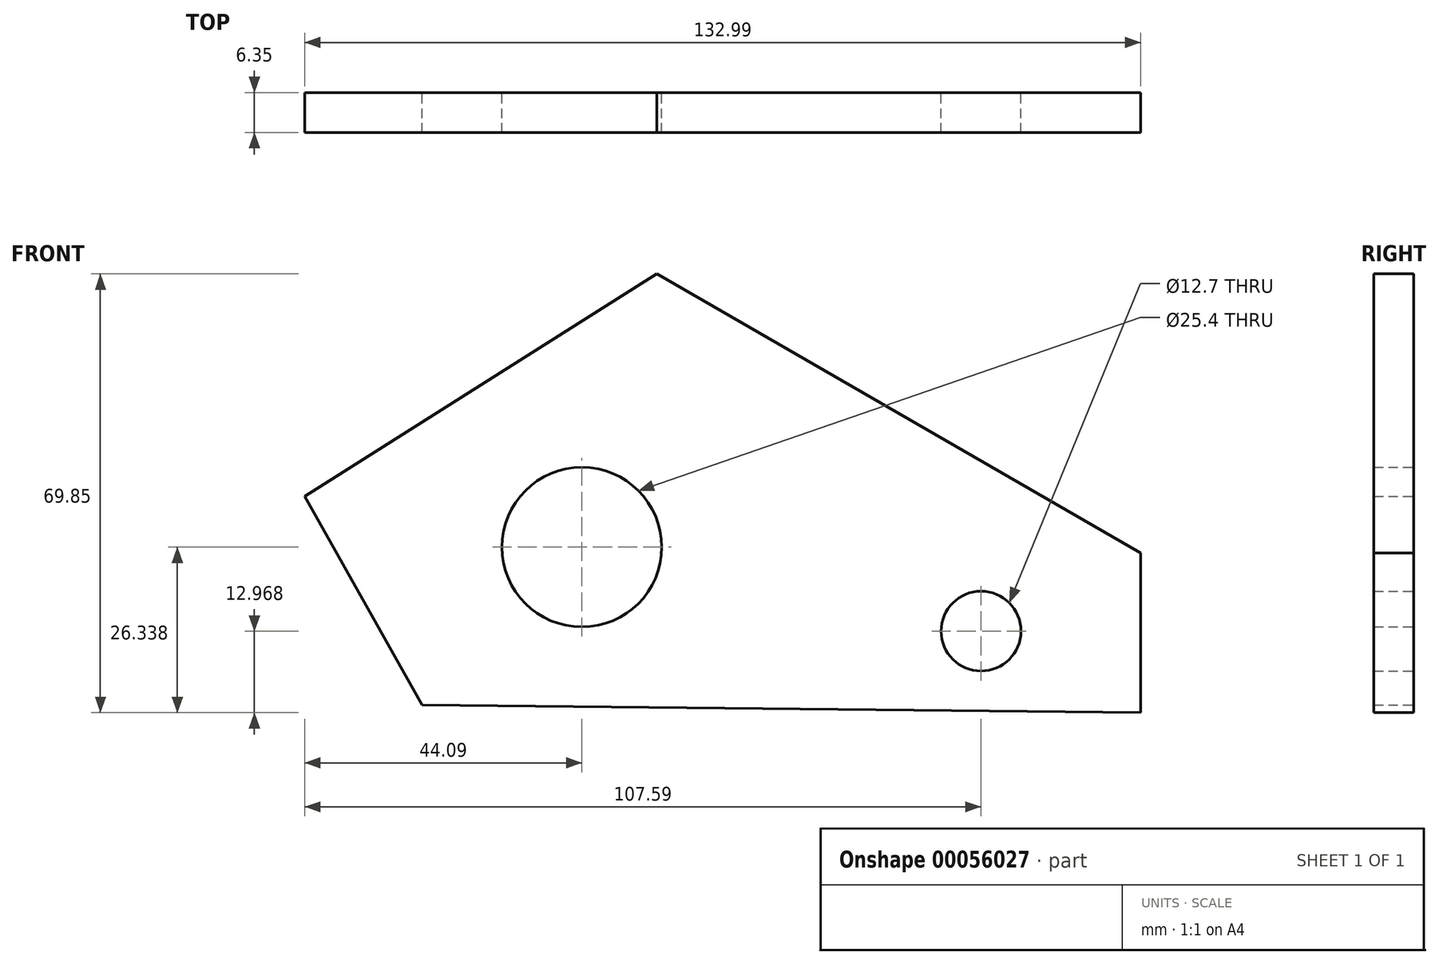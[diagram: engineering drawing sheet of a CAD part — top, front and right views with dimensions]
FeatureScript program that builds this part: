
annotation { "Feature Type Name" : "Feature", "Feature Type Description" : "" }
export const myFeature = defineFeature(function(context is Context, id is Id, definition is map)
    precondition{}
    {
        {
            var Q0;
            Q0=qCreatedBy(makeId("Front.planeOp"),FACE);
            var sketch = newSketch(context, id + "F0", { "sketchPlane" : qUnion([Q0])});
            skLineSegment(sketch, "E0", {"start": v(0, 25.4) * mm, "end": v(-76.99, 69.85) * mm});
            skLineSegment(sketch, "E1", {"start": v(-114.3, 1.2) * mm, "end": v(0, 0) * mm});
            skLineSegment(sketch, "E2", {"start": v(0, 25.4) * mm, "end": v(0, 0) * mm});
            skLineSegment(sketch, "E3", {"start": v(-76.99, 69.85) * mm, "end": v(-133, 34.4) * mm});
            skLineSegment(sketch, "E4", {"start": v(-133, 34.4) * mm, "end": v(-114.3, 1.2) * mm});
            skCircle(sketch, "E5", {"center": v(-25.4, 12.97) * mm, "radius": 6.35 * mm});
            skCircle(sketch, "E6", {"center": v(-88.9, 26.34) * mm, "radius": 12.7 * mm});
            skSolve(sketch);
        }
        {
            var Q0;
            Q0 = qSketchRegion(id + "F0", true);
            extrude(context, id + "F1", {"entities" : qUnion([Q0]), "depth" : 6.35 * mm});
        }
    });
